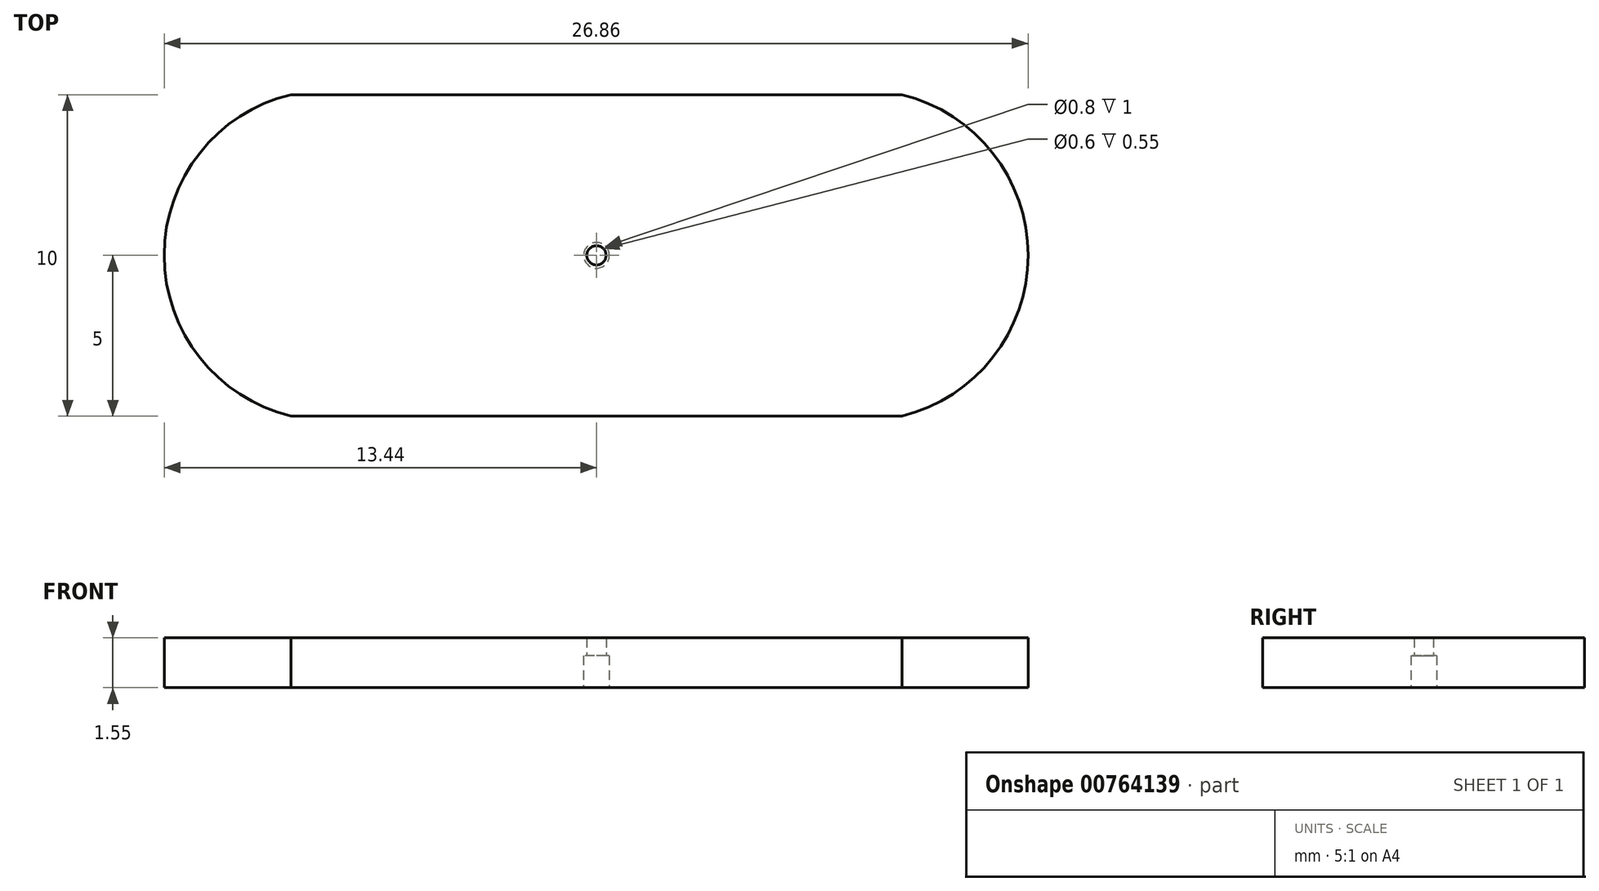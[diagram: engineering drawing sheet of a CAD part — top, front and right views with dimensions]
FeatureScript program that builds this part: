
annotation { "Feature Type Name" : "Feature", "Feature Type Description" : "" }
export const myFeature = defineFeature(function(context is Context, id is Id, definition is map)
    precondition{}
    {
        {
            var Q0;
            Q0=qCreatedBy(makeId("Top.planeOp"),FACE);
            var sketch = newSketch(context, id + "F0", { "sketchPlane" : qUnion([Q0])});
            skLineSegment(sketch, "E0.bottom", {"start": v(9.5, -5) * mm, "end": v(-9.5, -5) * mm});
            skLineSegment(sketch, "E0.top", {"start": v(9.5, 5) * mm, "end": v(-9.5, 5) * mm});
            skPoint(sketch, "E0.middle", {"position": v(0, 0) * mm});
            skLineSegment(sketch, "E1", {"start": v(-13.5, 16.08) * mm, "end": v(-13.5, -14.56) * mm, "construction": true});
            skLineSegment(sketch, "E2", {"start": v(13.5, 17.66) * mm, "end": v(13.5, -14.65) * mm, "construction": true});
            skArc(sketch, "E3", {"start": v(9.5, -5) * mm, "mid": v(13.42, 0) * mm, "end": v(9.5, 5) * mm});
            skArc(sketch, "E4", {"start": v(-9.5, 5) * mm, "mid": v(-13.44, 0) * mm, "end": v(-9.5, -5) * mm});
            skCircle(sketch, "E5", {"center": v(0, 0) * mm, "radius": 0.4 * mm});
            skSolve(sketch);
        }
        {
            var Q0;
            Q0=makeQuery(id+"F0.imprint","IMPRINT",FACE,{"disambiguationData":[TD([[makeQuery(id+"F0.imprint","IMPRINT",EDGE,{"derivedFrom":sQuery(id+"F0.wireOp",EDGE,"E0.bottom")}),-1.0]])]});
            extrude(context, id + "F1", {"entities" : qUnion([Q0]), "depth" : 1 * mm, "offsetDistance" : 25 * mm});
        }
        {
            var Q0;
            Q0=makeQuery(id+"F1.opExtrude","CAP_FACE",FACE,{"disambiguationData":[OSD([sQuery(id+"F0.wireOp",EDGE,"E0.bottom"),sQuery(id+"F0.wireOp",EDGE,"E0.top"),sQuery(id+"F0.wireOp",EDGE,"E3"),sQuery(id+"F0.wireOp",EDGE,"E4"),sQuery(id+"F0.wireOp",EDGE,"E5")])],"isStart":false});
            var sketch = newSketch(context, id + "F2", { "sketchPlane" : qUnion([Q0])});
            skArc(sketch, "E6.0", {"start": v(-9.5, 5) * mm, "mid": v(-13.44, 0) * mm, "end": v(-9.5, -5) * mm});
            skLineSegment(sketch, "E6.1", {"start": v(9.5, -5) * mm, "end": v(-9.5, -5) * mm});
            skArc(sketch, "E6.2", {"start": v(9.5, -5) * mm, "mid": v(13.42, 0) * mm, "end": v(9.5, 5) * mm});
            skLineSegment(sketch, "E6.3", {"start": v(9.5, 5) * mm, "end": v(-9.5, 5) * mm});
            skCircle(sketch, "E7", {"center": v(0, 0) * mm, "radius": 0.3 * mm});
            skSolve(sketch);
        }
        {
            var Q0;
            Q0 = qSketchRegion(id + "F2", true);
            extrude(context, id + "F3", {"entities" : qUnion([Q0]), "operationType" : NewBodyOperationType.ADD, "depth" : 0.55 * mm, "offsetDistance" : 25 * mm});
        }
    });
